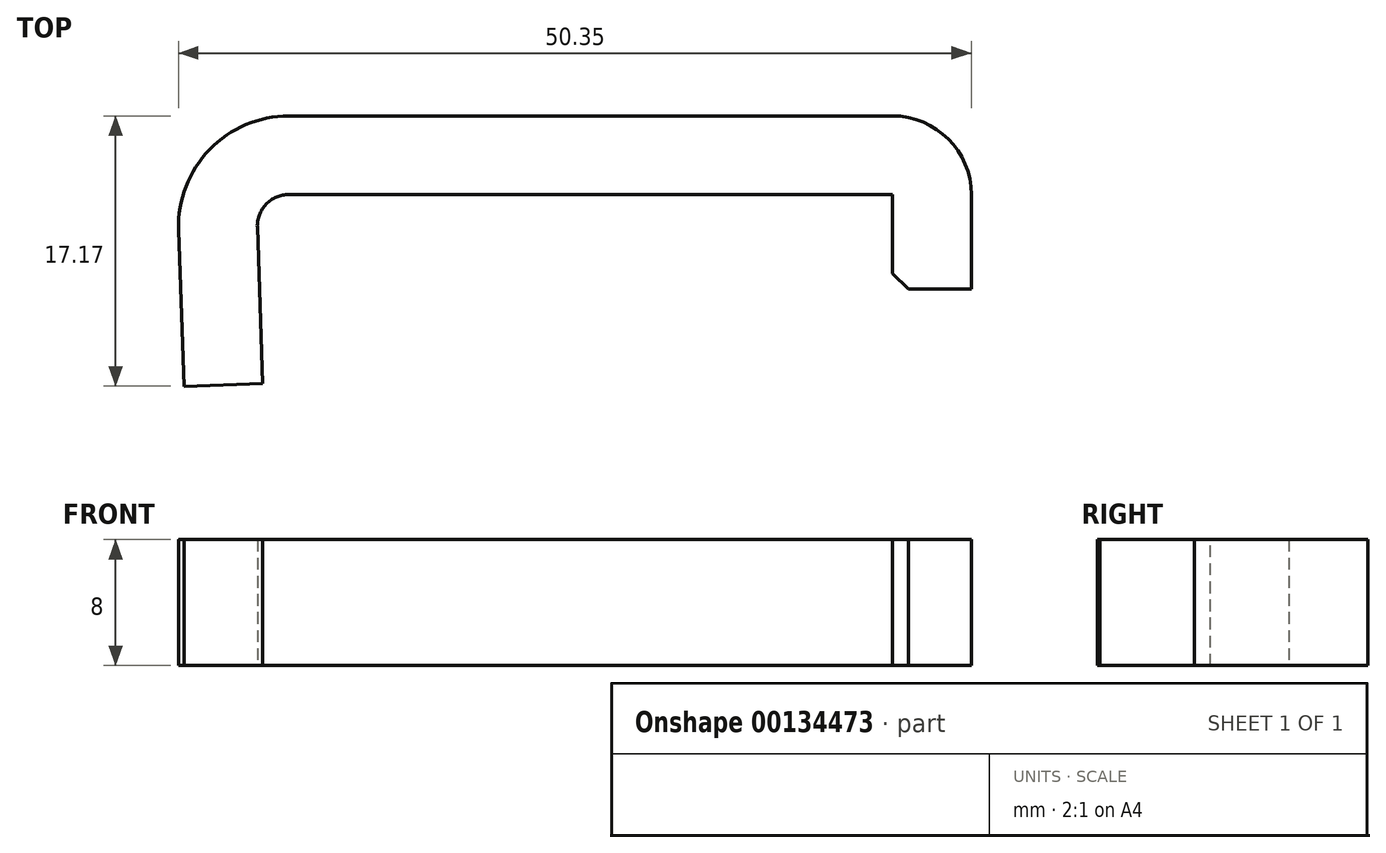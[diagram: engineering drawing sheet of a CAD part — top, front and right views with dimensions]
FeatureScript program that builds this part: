
annotation { "Feature Type Name" : "Feature", "Feature Type Description" : "" }
export const myFeature = defineFeature(function(context is Context, id is Id, definition is map)
    precondition{}
    {
        {
            var Q0;
            Q0=qCreatedBy(makeId("Top.planeOp"),FACE);
            var sketch = newSketch(context, id + "F0", { "sketchPlane" : qUnion([Q0])});
            skLineSegment(sketch, "E0", {"start": v(-40, -12) * mm, "end": v(-45, -12.17) * mm});
            skLineSegment(sketch, "E1", {"start": v(-45, -12.17) * mm, "end": v(-45.6, 5) * mm});
            skLineSegment(sketch, "E2", {"start": v(-45.6, 5) * mm, "end": v(5, 5) * mm});
            skLineSegment(sketch, "E3", {"start": v(5, 5) * mm, "end": v(5, -6) * mm});
            skLineSegment(sketch, "E4", {"start": v(5, -6) * mm, "end": v(0, -6) * mm});
            skLineSegment(sketch, "E5", {"start": v(0, -6) * mm, "end": v(0, 0) * mm});
            skLineSegment(sketch, "E6", {"start": v(0, 0) * mm, "end": v(-38.35, 0) * mm});
            skLineSegment(sketch, "E7", {"start": v(-40.35, -2.07) * mm, "end": v(-40, -12) * mm});
            skPoint(sketch, "E8.visualSharp", {"position": v(-40.42, 0) * mm});
            skArc(sketch, "E8.filletArc", {"start": v(-38.35, 0) * mm, "mid": v(-39.79, -0.61) * mm, "end": v(-40.35, -2.07) * mm});
            skSolve(sketch);
        }
        {
            var Q0;
            Q0 = qSketchRegion(id + "F0", true);
            extrude(context, id + "F1", {"entities" : qUnion([Q0]), "depth" : 8 * mm});
        }
        {
            var Q0;
            Q0=makeQuery(id+"F1.opExtrude","SWEPT_EDGE",EDGE,{"disambiguationData":[OSD([sQuery(id+"F0.wireOp",EDGE,"E4"),sQuery(id+"F0.wireOp",EDGE,"E5")])]});
            chamfer(context, id + "F2", {"entities" : qUnion([Q0]), "width" : 1 * mm, "tangentPropagation" : true});
        }
        {
            var Q0;
            Q0=makeQuery(id+"F1.opExtrude","SWEPT_EDGE",EDGE,{"disambiguationData":[OSD([sQuery(id+"F0.wireOp",EDGE,"E1"),sQuery(id+"F0.wireOp",EDGE,"E2")])]});
            fillet(context, id + "F3", {"entities" : qUnion([Q0]), "radius" : 7 * mm, "tangentPropagation" : true, "allowEdgeOverflow" : false});
        }
        {
            var Q0;
            Q0=makeQuery(id+"F1.opExtrude","SWEPT_EDGE",EDGE,{"disambiguationData":[OSD([sQuery(id+"F0.wireOp",EDGE,"E2"),sQuery(id+"F0.wireOp",EDGE,"E3")])]});
            fillet(context, id + "F4", {"entities" : qUnion([Q0]), "radius" : 5 * mm, "tangentPropagation" : true, "allowEdgeOverflow" : false});
        }
    });
